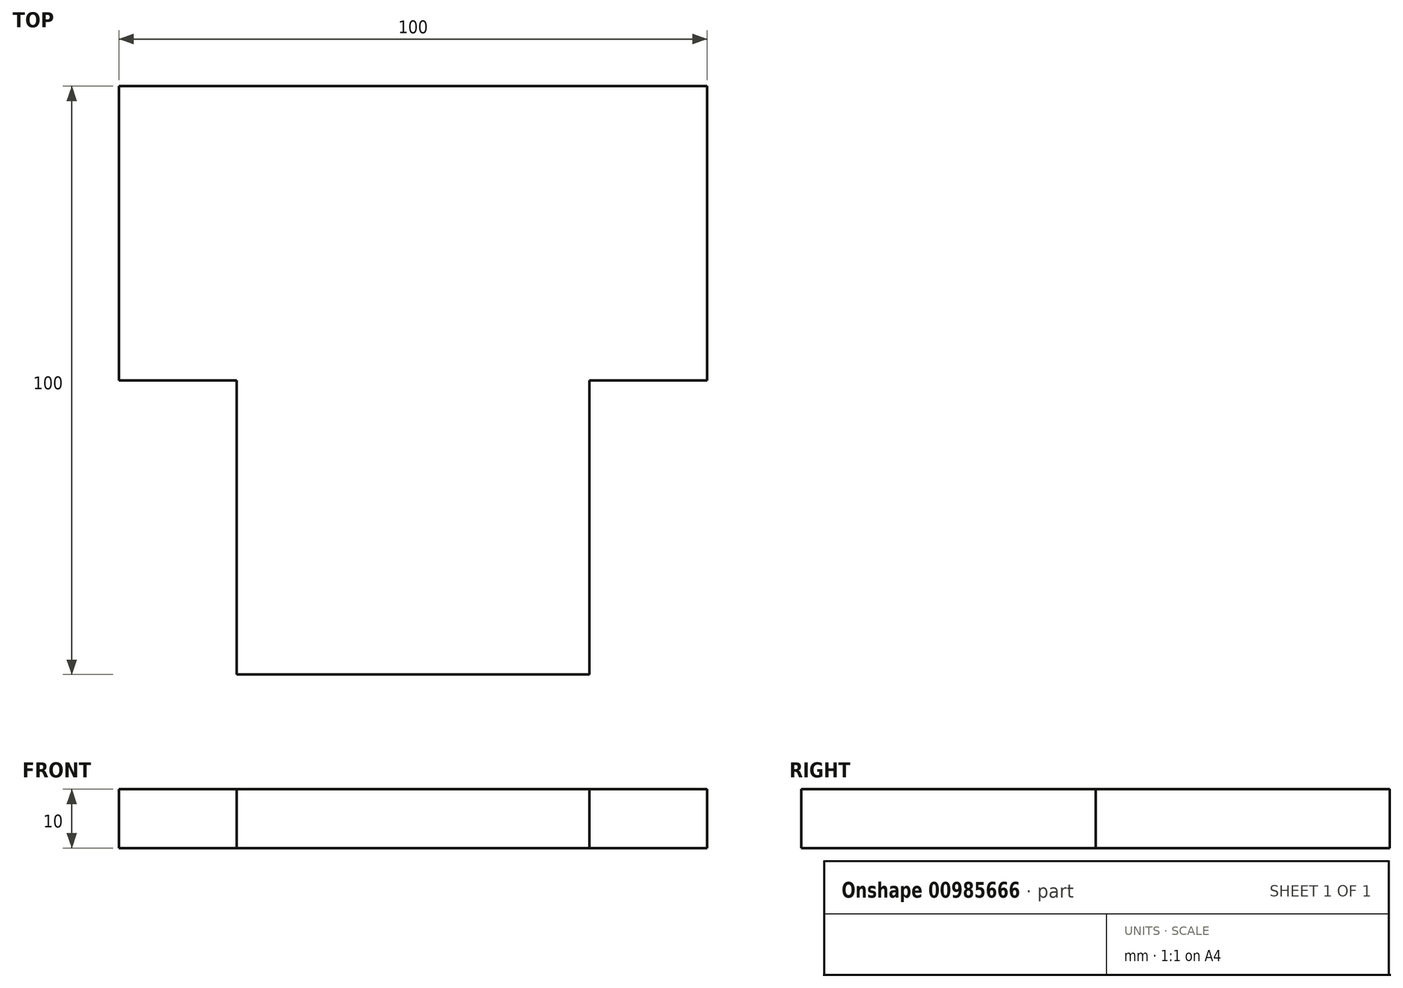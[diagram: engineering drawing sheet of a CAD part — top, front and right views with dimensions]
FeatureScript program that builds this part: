
annotation { "Feature Type Name" : "Feature", "Feature Type Description" : "" }
export const myFeature = defineFeature(function(context is Context, id is Id, definition is map)
    precondition{}
    {
        {
            var Q0;
            Q0=qCreatedBy(makeId("Top.planeOp"),FACE);
            var sketch = newSketch(context, id + "F0", { "sketchPlane" : qUnion([Q0])});
            skLineSegment(sketch, "E0.bottom", {"start": v(-44.18, 61.17) * mm, "end": v(55.82, 61.17) * mm});
            skLineSegment(sketch, "E0.top", {"start": v(-24.18, -38.83) * mm, "end": v(35.82, -38.83) * mm});
            skLineSegment(sketch, "E0.left", {"start": v(-44.18, 61.17) * mm, "end": v(-44.18, 11.17) * mm});
            skLineSegment(sketch, "E0.right", {"start": v(55.82, 61.17) * mm, "end": v(55.82, 11.17) * mm});
            skLineSegment(sketch, "E1", {"start": v(-24.18, -38.83) * mm, "end": v(-24.18, 11.17) * mm});
            skLineSegment(sketch, "E2", {"start": v(-24.18, 11.17) * mm, "end": v(-44.18, 11.17) * mm});
            skLineSegment(sketch, "E3", {"start": v(35.82, -38.83) * mm, "end": v(35.82, 11.17) * mm});
            skLineSegment(sketch, "E4", {"start": v(35.82, 11.17) * mm, "end": v(55.82, 11.17) * mm});
            skPoint(sketch, "E5.orphan", {"position": v(-44.18, -38.83) * mm});
            skPoint(sketch, "E6.orphan", {"position": v(55.82, -38.83) * mm});
            skSolve(sketch);
        }
        {
            var Q0;
            Q0 = qSketchRegion(id + "F0", true);
            extrude(context, id + "F1", {"entities" : qUnion([Q0]), "depth" : 10 * mm, "offsetDistance" : 25 * mm});
        }
    });
